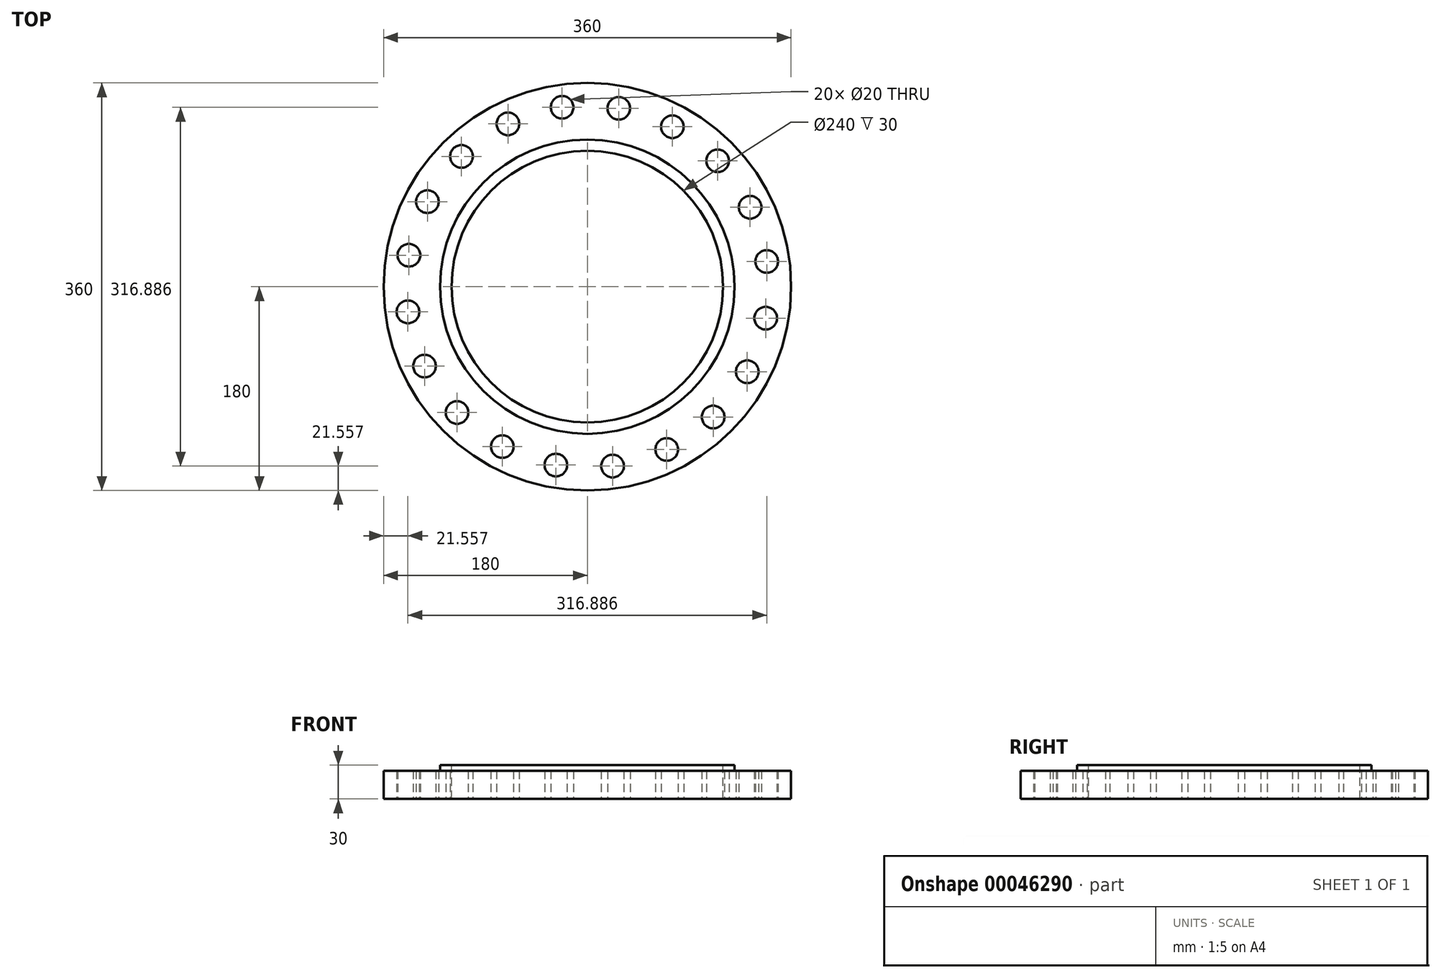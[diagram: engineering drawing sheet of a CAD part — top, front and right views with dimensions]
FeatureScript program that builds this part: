
annotation { "Feature Type Name" : "Feature", "Feature Type Description" : "" }
export const myFeature = defineFeature(function(context is Context, id is Id, definition is map)
    precondition{}
    {
        {
            var Q0;
            Q0=qCreatedBy(makeId("Top.planeOp"),FACE);
            var sketch = newSketch(context, id + "F0", { "sketchPlane" : qUnion([Q0])});
            skCircle(sketch, "E0", {"center": v(0, 0) * mm, "radius": 180 * mm});
            skCircle(sketch, "E1", {"center": v(0, 0) * mm, "radius": 160 * mm, "construction": true});
            skLineSegment(sketch, "E2", {"start": v(0, 0) * mm, "end": v(0, 160) * mm, "construction": true});
            skLineSegment(sketch, "E3", {"start": v(0, 0) * mm, "end": v(33.77, 191.5) * mm, "construction": true});
            skCircle(sketch, "E4", {"center": v(27.78, 157.57) * mm, "radius": 10 * mm});
            skCircle(sketch, "E5.1.0", {"center": v(-22.27, 158.44) * mm, "radius": 10 * mm});
            skCircle(sketch, "E5.2.0", {"center": v(-70.14, 143.8) * mm, "radius": 10 * mm});
            skCircle(sketch, "E5.3.0", {"center": v(-111.15, 115.1) * mm, "radius": 10 * mm});
            skCircle(sketch, "E5.4.0", {"center": v(-141.27, 75.12) * mm, "radius": 10 * mm});
            skCircle(sketch, "E5.5.0", {"center": v(-157.57, 27.78) * mm, "radius": 10 * mm});
            skCircle(sketch, "E5.6.0", {"center": v(-158.44, -22.27) * mm, "radius": 10 * mm});
            skCircle(sketch, "E5.7.0", {"center": v(-143.8, -70.14) * mm, "radius": 10 * mm});
            skCircle(sketch, "E5.8.0", {"center": v(-115.1, -111.15) * mm, "radius": 10 * mm});
            skCircle(sketch, "E5.9.0", {"center": v(-75.12, -141.27) * mm, "radius": 10 * mm});
            skCircle(sketch, "E5.10.0", {"center": v(-27.78, -157.57) * mm, "radius": 10 * mm});
            skCircle(sketch, "E5.11.0", {"center": v(22.27, -158.44) * mm, "radius": 10 * mm});
            skCircle(sketch, "E5.12.0", {"center": v(70.14, -143.8) * mm, "radius": 10 * mm});
            skCircle(sketch, "E5.13.0", {"center": v(111.15, -115.1) * mm, "radius": 10 * mm});
            skCircle(sketch, "E5.14.0", {"center": v(141.27, -75.12) * mm, "radius": 10 * mm});
            skCircle(sketch, "E5.15.0", {"center": v(157.57, -27.78) * mm, "radius": 10 * mm});
            skCircle(sketch, "E5.16.0", {"center": v(158.44, 22.27) * mm, "radius": 10 * mm});
            skCircle(sketch, "E5.17.0", {"center": v(143.8, 70.14) * mm, "radius": 10 * mm});
            skCircle(sketch, "E5.18.0", {"center": v(115.1, 111.15) * mm, "radius": 10 * mm});
            skCircle(sketch, "E5.19.0", {"center": v(75.12, 141.27) * mm, "radius": 10 * mm});
            skSolve(sketch);
        }
        {
            var Q0;
            Q0=makeQuery(id+"F0.imprint","IMPRINT",FACE,{"disambiguationData":[TD([[makeQuery(id+"F0.imprint","IMPRINT",EDGE,{"derivedFrom":sQuery(id+"F0.wireOp",EDGE,"E0")}),1.0]])]});
            extrude(context, id + "F1", {"entities" : qUnion([Q0]), "depth" : 25 * mm});
        }
        {
            var Q0;
            Q0=makeQuery(id+"F1.opExtrude","CAP_FACE",FACE,{"disambiguationData":[OSD([sQuery(id+"F0.wireOp",EDGE,"E0"),sQuery(id+"F0.wireOp",EDGE,"E4"),sQuery(id+"F0.wireOp",EDGE,"E5.1.0"),sQuery(id+"F0.wireOp",EDGE,"E5.2.0"),sQuery(id+"F0.wireOp",EDGE,"E5.3.0"),sQuery(id+"F0.wireOp",EDGE,"E5.4.0"),sQuery(id+"F0.wireOp",EDGE,"E5.5.0"),sQuery(id+"F0.wireOp",EDGE,"E5.6.0"),sQuery(id+"F0.wireOp",EDGE,"E5.7.0"),sQuery(id+"F0.wireOp",EDGE,"E5.8.0"),sQuery(id+"F0.wireOp",EDGE,"E5.9.0"),sQuery(id+"F0.wireOp",EDGE,"E5.10.0"),sQuery(id+"F0.wireOp",EDGE,"E5.11.0"),sQuery(id+"F0.wireOp",EDGE,"E5.12.0"),sQuery(id+"F0.wireOp",EDGE,"E5.13.0"),sQuery(id+"F0.wireOp",EDGE,"E5.14.0"),sQuery(id+"F0.wireOp",EDGE,"E5.15.0"),sQuery(id+"F0.wireOp",EDGE,"E5.16.0"),sQuery(id+"F0.wireOp",EDGE,"E5.17.0"),sQuery(id+"F0.wireOp",EDGE,"E5.18.0"),sQuery(id+"F0.wireOp",EDGE,"E5.19.0")])],"isStart":false});
            var sketch = newSketch(context, id + "F2", { "sketchPlane" : qUnion([Q0])});
            skCircle(sketch, "E6", {"center": v(0, 0) * mm, "radius": 130 * mm});
            skSolve(sketch);
        }
        {
            var Q0;
            Q0 = qSketchRegion(id + "F2", true);
            var Q1;
            Q1=makeQuery(id+"F2.imprint","IMPRINT",FACE,{"disambiguationData":[TD([[makeQuery(id+"F2.imprint","IMPRINT",EDGE,{"derivedFrom":sQuery(id+"F2.wireOp",EDGE,"E6")}),1.0]])]});
            extrude(context, id + "F3", {"entities" : qUnion([Q0, Q1]), "operationType" : NewBodyOperationType.ADD, "depth" : 5 * mm});
        }
        {
            var Q0;
            Q0=makeQuery(id+"F3.opExtrude","CAP_FACE",FACE,{"disambiguationData":[OSD([sQuery(id+"F2.wireOp",EDGE,"E6")])],"isStart":false});
            var sketch = newSketch(context, id + "F4", { "sketchPlane" : qUnion([Q0])});
            skCircle(sketch, "E7", {"center": v(0, 0) * mm, "radius": 120 * mm});
            skSolve(sketch);
        }
        {
            var Q0;
            Q0 = qSketchRegion(id + "F4", true);
            var Q1;
            Q1=makeQuery(id+"F4.imprint","IMPRINT",FACE,{"disambiguationData":[TD([[makeQuery(id+"F4.imprint","IMPRINT",EDGE,{"derivedFrom":sQuery(id+"F4.wireOp",EDGE,"E7")}),1.0]])]});
            extrude(context, id + "F5", {"entities" : qUnion([Q0, Q1]), "operationType" : NewBodyOperationType.REMOVE, "endBound" : BoundingType.THROUGH_ALL, "oppositeDirection" : true, "depth" : 25 * mm});
        }
    });
